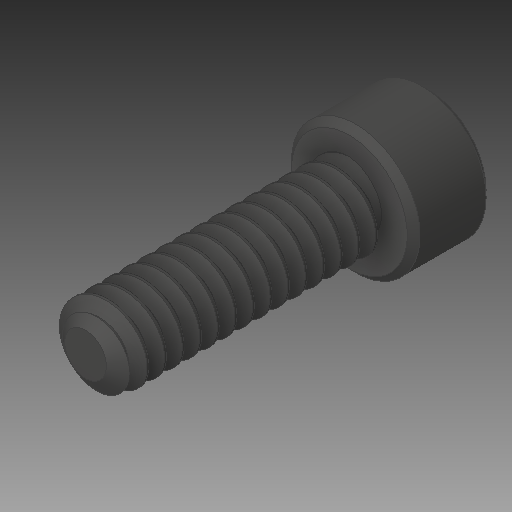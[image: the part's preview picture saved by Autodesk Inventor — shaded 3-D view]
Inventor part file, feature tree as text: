
AUTODESK INVENTOR PART (.ipt)
format: ipt  version: 2017 (Build 210142000, 142)  size: 697,856 bytes
history: native  units: in
note: dims shown in document units (in); Inventor stores cm internally (conversion verified against a paired STEP export)
features: chamfer x1
ambient origin geometry x8: Origin, YZ Plane, XZ Plane, XY Plane, X Axis, Y Axis, Z Axis, Center Point
bodies: Solid1 (feature_tree)
feature tree (1):
  chamfer  "Chamfer1"  [1 undecoded]
note: 1 required parameter value undecoded (feature->parameter linkage not recoverable at this tier; creation-order binding heuristic only, values carry confidence <= 0.55)
